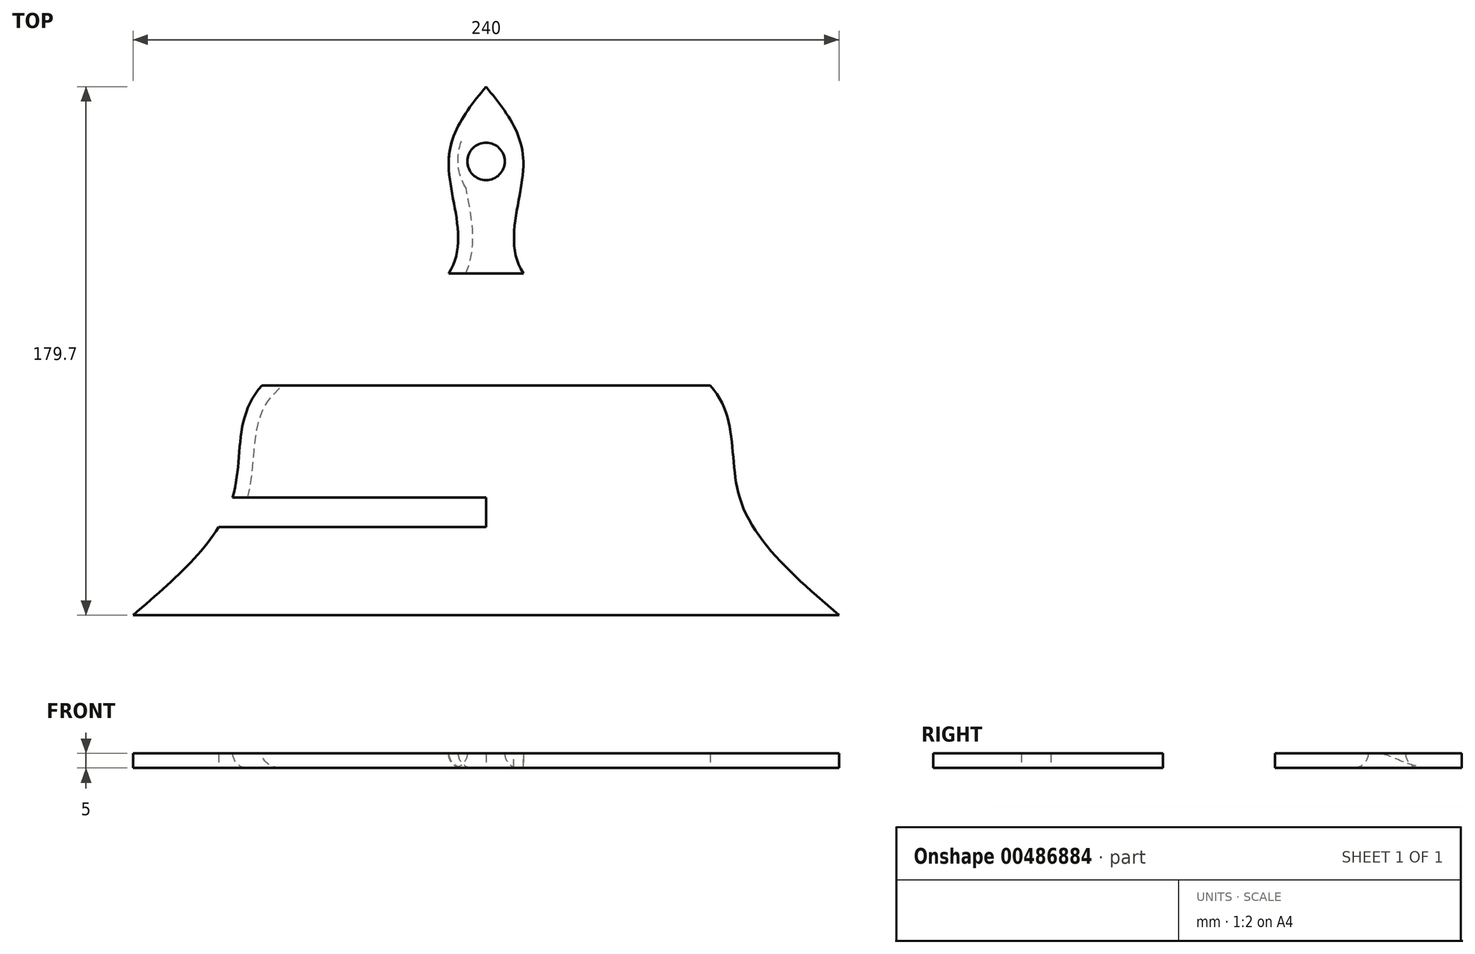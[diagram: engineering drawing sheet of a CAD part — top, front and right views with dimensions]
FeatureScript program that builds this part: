
annotation { "Feature Type Name" : "Feature", "Feature Type Description" : "" }
export const myFeature = defineFeature(function(context is Context, id is Id, definition is map)
    precondition{}
    {
        {
            var Q0;
            Q0=qCreatedBy(makeId("Top.planeOp"),FACE);
            var sketch = newSketch(context, id + "F0", { "sketchPlane" : qUnion([Q0])});
            skLineSegment(sketch, "E0", {"start": v(0, 0) * mm, "end": v(-12.7, 0) * mm});
            skLineSegment(sketch, "E1", {"start": v(-12.7, 0) * mm, "end": v(12.7, 0) * mm});
            skLineSegment(sketch, "E2", {"start": v(0, 0) * mm, "end": v(0, -76.2) * mm});
            skLineSegment(sketch, "E3", {"start": v(0, -76.2) * mm, "end": v(-76.2, -76.2) * mm});
            skLineSegment(sketch, "E4", {"start": v(-76.2, -76.2) * mm, "end": v(76.2, -76.2) * mm});
            skLineSegment(sketch, "E5", {"start": v(76.2, -76.2) * mm, "end": v(76.2, -38.1) * mm});
            skLineSegment(sketch, "E6", {"start": v(76.2, -38.1) * mm, "end": v(-76.2, -38.1) * mm});
            skLineSegment(sketch, "E7", {"start": v(0, 0) * mm, "end": v(0, 63.5) * mm});
            skLineSegment(sketch, "E8", {"start": v(-12.7, 0) * mm, "end": v(-12.7, 38.1) * mm});
            skLineSegment(sketch, "E9", {"start": v(-12.7, 38.1) * mm, "end": v(12.7, 38.1) * mm});
            skCircle(sketch, "E10", {"center": v(0, 38.1) * mm, "radius": 6.35 * mm});
            skLineSegment(sketch, "E11", {"start": v(0, -76.2) * mm, "end": v(0, -116.2) * mm});
            skLineSegment(sketch, "E12", {"start": v(-76.2, -76.2) * mm, "end": v(-86.2, -76.2) * mm});
            skLineSegment(sketch, "E13", {"start": v(76.2, -76.2) * mm, "end": v(86.2, -76.2) * mm});
            skLineSegment(sketch, "E14", {"start": v(0, -116.2) * mm, "end": v(-120, -116.2) * mm});
            skLineSegment(sketch, "E15", {"start": v(-120, -116.2) * mm, "end": v(120, -116.2) * mm});
            skFitSpline(sketch, "E16", {"points": [v(0, 63.5) * mm, v(-12.7, 38.1) * mm, v(-12.7, 0) * mm, v(-76.2, -38.1) * mm, v(-86.2, -76.2) * mm, v(-120, -116.2) * mm], "startDerivative": vector(-117.69, -144.23) * mm, "endDerivative": vector(-204.5, -175.6) * mm});
            skFitSpline(sketch, "E17", {"points": [v(0, 63.5) * mm, v(12.7, 38.1) * mm, v(12.7, 0) * mm, v(76.2, -38.1) * mm, v(86.2, -76.2) * mm, v(120, -116.2) * mm], "startDerivative": vector(117.69, -144.23) * mm, "endDerivative": vector(204.5, -175.6) * mm});
            skLineSegment(sketch, "E18", {"start": v(0, -76.2) * mm, "end": v(0, -78.1) * mm});
            skLineSegment(sketch, "E19", {"start": v(0, -38.1) * mm, "end": v(0, -28.1) * mm});
            skLineSegment(sketch, "E20", {"start": v(0, -28.1) * mm, "end": v(0, -48.1) * mm});
            skLineSegment(sketch, "E21", {"start": v(0, -48.1) * mm, "end": v(0, -58.1) * mm});
            skLineSegment(sketch, "E22", {"start": v(0, -58.1) * mm, "end": v(0, -68.1) * mm});
            skLineSegment(sketch, "E23", {"start": v(0, -68.1) * mm, "end": v(0, -78.1) * mm});
            skLineSegment(sketch, "E24", {"start": v(0, -76.2) * mm, "end": v(0, -86.2) * mm});
            skLineSegment(sketch, "E25", {"start": v(0, -86.2) * mm, "end": v(0, -96.2) * mm});
            skLineSegment(sketch, "E26", {"start": v(0, -96.2) * mm, "end": v(0, -106.2) * mm});
            skLineSegment(sketch, "E27", {"start": v(0, -106.2) * mm, "end": v(-101, -106.2) * mm});
            skLineSegment(sketch, "E28", {"start": v(-101, -106.2) * mm, "end": v(101, -106.2) * mm});
            skLineSegment(sketch, "E29", {"start": v(0, -96.2) * mm, "end": v(-97, -96.2) * mm});
            skLineSegment(sketch, "E30", {"start": v(-97, -96.2) * mm, "end": v(97, -96.2) * mm});
            skLineSegment(sketch, "E31", {"start": v(0, -86.2) * mm, "end": v(-93, -86.2) * mm});
            skSolve(sketch);
        }
        {
            var Q0;
            Q0=sQuery(id+"F0.wireOp",EDGE,"E17");
            var Q1;
            Q1=sQuery(id+"F0.wireOp",EDGE,"E16");
            extrude(context, id + "F1", {"bodyType" : ToolBodyType.SURFACE, "surfaceEntities" : qUnion([Q0, Q1]), "depth" : 25 * mm});
        }
        {
            var Q0;
            {var subQ1=sQuery(id+"F0.wireOp",EDGE,"E7");var subQ3=sQuery(id+"F0.wireOp",EDGE,"E10");var subQ4=makeQuery(id+"F0.imprint","INTERSECT",VERTEX,{"disambiguationData":[OD(1.0)],"derivedFrom":[subQ1,subQ3]});Q0=makeQuery(id+"F0.imprint","IMPRINT",FACE,{"disambiguationData":[TD([[makeQuery(id+"F0.imprint","IMPRINT",EDGE,{"disambiguationData":[TD([[subQ4,-1.0]])],"derivedFrom":subQ3}),-1.0]])]});}
            var Q1;
            {var subQ4=sQuery(id+"F0.wireOp",EDGE,"E10");var subQ7=sQuery(id+"F0.wireOp",EDGE,"E7");var subQ10=makeQuery(id+"F0.imprint","INTERSECT",VERTEX,{"disambiguationData":[OD(0.0)],"derivedFrom":[subQ7,subQ4]});Q1=makeQuery(id+"F0.imprint","IMPRINT",FACE,{"disambiguationData":[TD([[makeQuery(id+"F0.imprint","IMPRINT",EDGE,{"disambiguationData":[TD([[subQ10,1.0]])],"derivedFrom":subQ4}),-1.0]])]});}
            var Q2;
            {var subQ0=sQuery(id+"F0.wireOp",EDGE,"E17");var subQ1=sQuery(id+"F0.wireOp",EDGE,"E9");var subQ2=makeQuery(id+"F0.imprint","INTERSECT",VERTEX,{"derivedFrom":[subQ1,subQ0]});Q2=makeQuery(id+"F0.imprint","IMPRINT",FACE,{"disambiguationData":[TD([[makeQuery(id+"F0.imprint","IMPRINT",EDGE,{"disambiguationData":[TD([[subQ2,1.0]])],"derivedFrom":subQ1}),-1.0]])]});}
            var Q3;
            {var subQ5=sQuery(id+"F0.wireOp",EDGE,"E2");Q3=makeQuery(id+"F0.imprint","IMPRINT",FACE,{"disambiguationData":[TD([[makeQuery(id+"F0.imprint","IMPRINT",EDGE,{"derivedFrom":subQ5}),1.0]])]});}
            var Q4;
            {var subQ5=sQuery(id+"F0.wireOp",EDGE,"E2");Q4=makeQuery(id+"F0.imprint","IMPRINT",FACE,{"disambiguationData":[TD([[makeQuery(id+"F0.imprint","IMPRINT",EDGE,{"derivedFrom":subQ5}),-1.0]])]});}
            var Q5;
            {var subQ3=sQuery(id+"F0.wireOp",EDGE,"E12");Q5=makeQuery(id+"F0.imprint","IMPRINT",FACE,{"disambiguationData":[TD([[makeQuery(id+"F0.imprint","IMPRINT",EDGE,{"derivedFrom":subQ3}),-1.0]])]});}
            var Q6;
            {var subQ1=sQuery(id+"F0.wireOp",EDGE,"E5");Q6=makeQuery(id+"F0.imprint","IMPRINT",FACE,{"disambiguationData":[TD([[makeQuery(id+"F0.imprint","IMPRINT",EDGE,{"derivedFrom":subQ1}),1.0]])]});}
            var Q7;
            {var subQ1=sQuery(id+"F0.wireOp",EDGE,"E11");Q7=makeQuery(id+"F0.imprint","IMPRINT",FACE,{"disambiguationData":[TD([[makeQuery(id+"F0.imprint","IMPRINT",EDGE,{"derivedFrom":subQ1}),1.0]])]});}
            var Q8;
            {var subQ1=sQuery(id+"F0.wireOp",EDGE,"E11");Q8=makeQuery(id+"F0.imprint","IMPRINT",FACE,{"disambiguationData":[TD([[makeQuery(id+"F0.imprint","IMPRINT",EDGE,{"derivedFrom":subQ1}),-1.0]])]});}
            var Q9;
            {var subQ0=sQuery(id+"F0.wireOp",EDGE,"E17");var subQ5=sQuery(id+"F0.wireOp",EDGE,"E9");var subQ6=makeQuery(id+"F0.imprint","INTERSECT",VERTEX,{"derivedFrom":[subQ5,subQ0]});Q9=makeQuery(id+"F0.imprint","IMPRINT",FACE,{"disambiguationData":[TD([[makeQuery(id+"F0.imprint","IMPRINT",EDGE,{"disambiguationData":[TD([[subQ6,1.0]])],"derivedFrom":subQ5}),1.0]])]});}
            var Q10;
            {var subQ0=sQuery(id+"F0.wireOp",EDGE,"E5");Q10=makeQuery(id+"F0.imprint","IMPRINT",FACE,{"disambiguationData":[TD([[makeQuery(id+"F0.imprint","IMPRINT",EDGE,{"derivedFrom":subQ0}),-1.0]])]});}
            extrude(context, id + "F2", {"entities" : qUnion([Q0, Q1, Q2, Q3, Q4, Q5, Q6, Q7, Q8, Q9, Q10]), "depth" : 5 * mm});
        }
        {
            var Q0;
            {var subQ0=sQuery(id+"F0.wireOp",EDGE,"E16");var subQ1=makeQuery(id+"F0.imprint","INTERSECT",VERTEX,{"derivedFrom":[sQuery(id+"F0.wireOp",EDGE,"E12"),subQ0]});var subQ2=makeQuery(id+"F0.imprint","INTERSECT",VERTEX,{"derivedFrom":[sQuery(id+"F0.wireOp",EDGE,"E6"),subQ0]});var subQ3=sQuery(id+"F0.wireOp",EDGE,"E8");Q0=makeQuery(id+"F2.opExtrude","CAP_EDGE",EDGE,{"disambiguationData":[OSD([subQ0]),TDD([makeQuery(id+"F0.imprint","IMPRINT",EDGE,{"disambiguationData":[TD([[makeQuery(id+"F0.imprint","INTERSECT",VERTEX,{"derivedFrom":[subQ3,subQ0]}),-1.0]])],"derivedFrom":subQ0}),makeQuery(id+"F0.imprint","IMPRINT",EDGE,{"disambiguationData":[TD([[subQ2,1.0]])],"derivedFrom":subQ0}),makeQuery(id+"F0.imprint","IMPRINT",EDGE,{"disambiguationData":[TD([[subQ2,-1.0]])],"derivedFrom":subQ0}),makeQuery(id+"F0.imprint","IMPRINT",EDGE,{"disambiguationData":[TD([[subQ1,-1.0]])],"derivedFrom":subQ0})])],"isStart":true});}
            var Q1;
            Q1=makeQuery(id+"F2.opExtrude","CAP_EDGE",EDGE,{"disambiguationData":[OSD([sQuery(id+"F0.wireOp",EDGE,"E10")])],"isStart":true});
            var Q2;
            Q2=makeQuery(id+"F1.opExtrude","SWEPT_FACE",FACE,{"disambiguationData":[OSD([sQuery(id+"F0.wireOp",EDGE,"E17")])]});
            fillet(context, id + "F3", {"entities" : qUnion([Q0, Q1, Q2]), "radius" : 5 * mm, "tangentPropagation" : true, "allowEdgeOverflow" : false});
        }
    });
